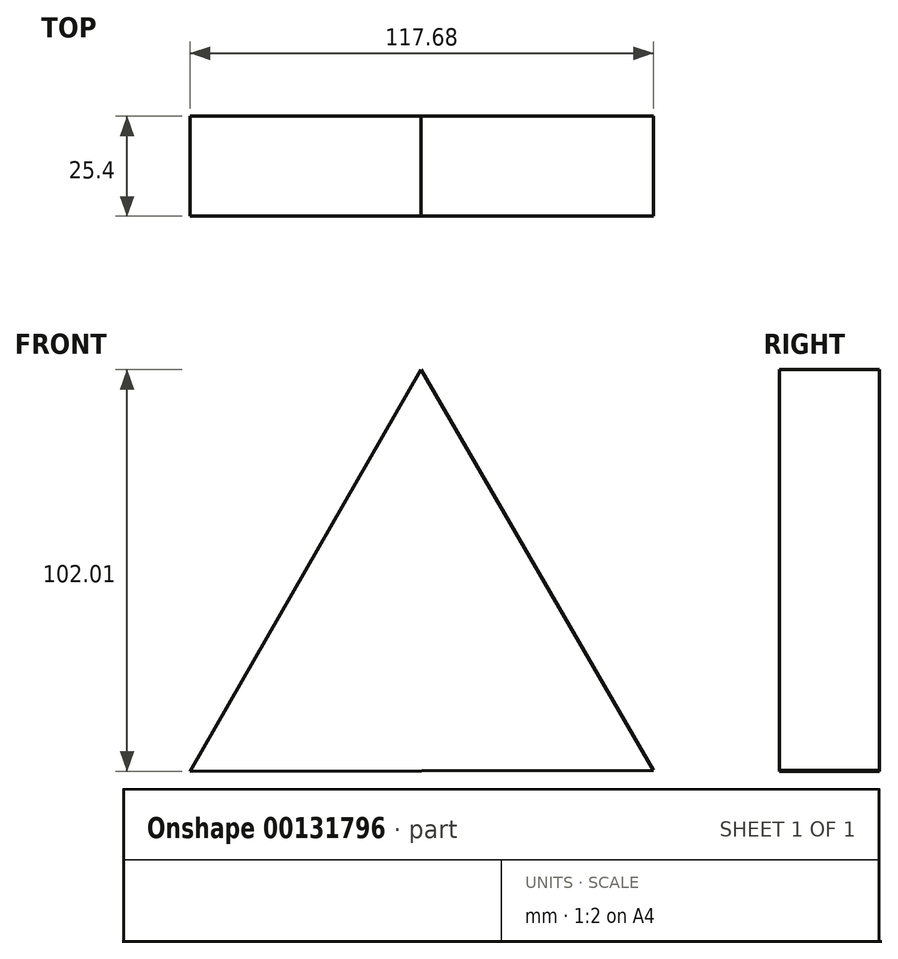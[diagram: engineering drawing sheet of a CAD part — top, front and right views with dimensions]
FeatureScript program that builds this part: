
annotation { "Feature Type Name" : "Feature", "Feature Type Description" : "" }
export const myFeature = defineFeature(function(context is Context, id is Id, definition is map)
    precondition{}
    {
        {
            var Q0;
            Q0=qCreatedBy(makeId("Front.planeOp"),FACE);
            var sketch = newSketch(context, id + "F0", { "sketchPlane" : qUnion([Q0])});
            skCircle(sketch, "E0.cCircle", {"center": v(0, -13.63) * mm, "radius": 33.97 * mm, "construction": true});
            skLineSegment(sketch, "E0.0", {"start": v(58.9, -47.5) * mm, "end": v(-58.78, -47.7) * mm});
            skLineSegment(sketch, "E0.1", {"start": v(-58.78, -47.7) * mm, "end": v(-0.12, 54.31) * mm});
            skLineSegment(sketch, "E0.2", {"start": v(-0.12, 54.31) * mm, "end": v(58.9, -47.5) * mm});
            skPoint(sketch, "E0.0.midPoint", {"position": v(0.06, -47.6) * mm});
            skSolve(sketch);
        }
        {
            var Q0;
            Q0=makeQuery(id+"F0.imprint","IMPRINT",FACE,{"disambiguationData":[TD([[makeQuery(id+"F0.imprint","IMPRINT",EDGE,{"derivedFrom":sQuery(id+"F0.wireOp",EDGE,"E0.0")}),-1.0]])]});
            extrude(context, id + "F1", {"entities" : qUnion([Q0]), "depth" : 25.4 * mm});
        }
    });
